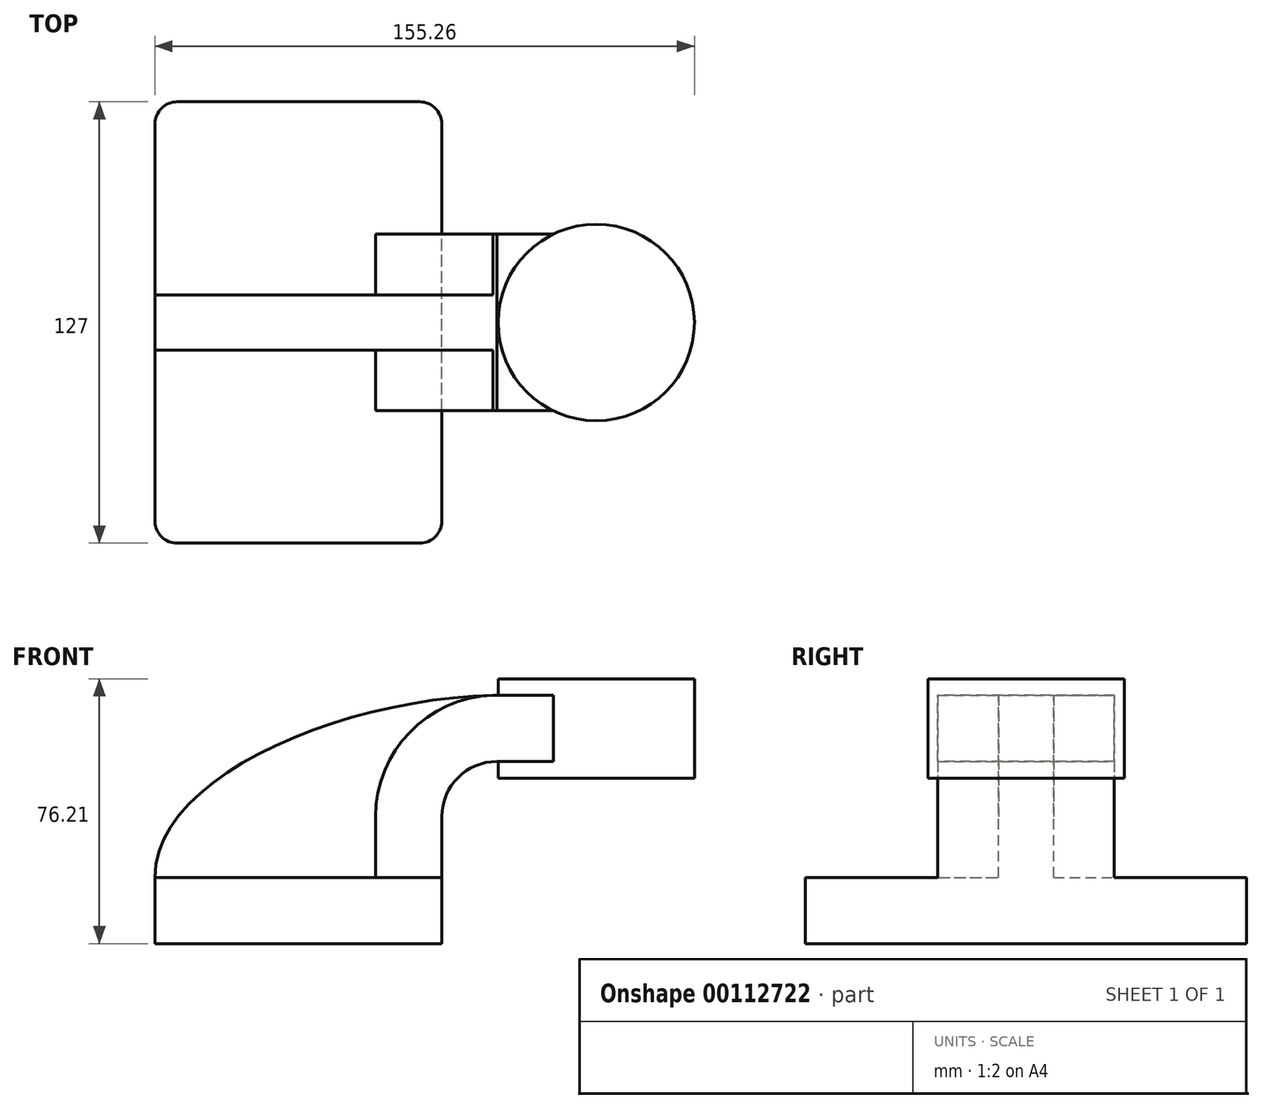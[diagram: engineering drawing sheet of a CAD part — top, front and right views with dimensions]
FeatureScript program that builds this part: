
annotation { "Feature Type Name" : "Feature", "Feature Type Description" : "" }
export const myFeature = defineFeature(function(context is Context, id is Id, definition is map)
    precondition{}
    {
        {
            var Q0;
            Q0=qCreatedBy(makeId("Front.planeOp"),FACE);
            var sketch = newSketch(context, id + "F0", { "sketchPlane" : qUnion([Q0])});
            skLineSegment(sketch, "E0.bottom", {"start": v(-41.28, -9.53) * mm, "end": v(41.28, -9.53) * mm});
            skLineSegment(sketch, "E0.top", {"start": v(-41.28, 9.53) * mm, "end": v(41.28, 9.53) * mm});
            skLineSegment(sketch, "E0.left", {"start": v(-41.28, -9.53) * mm, "end": v(-41.28, 9.53) * mm});
            skLineSegment(sketch, "E0.right", {"start": v(41.28, -9.53) * mm, "end": v(41.28, 9.53) * mm});
            skPoint(sketch, "E0.middle", {"position": v(0, 0) * mm});
            skLineSegment(sketch, "E1.bottom", {"start": v(63.18, 38.1) * mm, "end": v(113.98, 38.1) * mm});
            skLineSegment(sketch, "E1.top", {"start": v(63.18, 66.67) * mm, "end": v(113.98, 66.67) * mm});
            skLineSegment(sketch, "E1.left", {"start": v(63.18, 38.1) * mm, "end": v(63.18, 66.67) * mm});
            skLineSegment(sketch, "E1.right", {"start": v(113.98, 38.1) * mm, "end": v(113.98, 66.67) * mm});
            skPoint(sketch, "E1.middle", {"position": v(88.58, 52.39) * mm});
            skLineSegment(sketch, "E2", {"start": v(41.27, 9.53) * mm, "end": v(41.27, 27) * mm});
            skArc(sketch, "E3", {"start": v(41.27, 27) * mm, "mid": v(45.92, 38.23) * mm, "end": v(57.15, 42.88) * mm});
            skLineSegment(sketch, "E4", {"start": v(57.15, 42.88) * mm, "end": v(85.72, 42.88) * mm});
            skLineSegment(sketch, "E5.0", {"start": v(57.15, 61.93) * mm, "end": v(85.72, 61.93) * mm});
            skArc(sketch, "E5.1", {"start": v(22.23, 27) * mm, "mid": v(32.45, 51.7) * mm, "end": v(57.15, 61.93) * mm});
            skLineSegment(sketch, "E5.2", {"start": v(22.22, 9.53) * mm, "end": v(22.22, 27) * mm});
            skLineSegment(sketch, "E6", {"start": v(85.72, 66.67) * mm, "end": v(85.72, 38.1) * mm});
            skFitSpline(sketch, "E7", {"points": [v(-41.28, 9.53) * mm, v(57.15, 61.93) * mm], "startDerivative": vector(-0.7, 87.75) * mm, "endDerivative": vector(130.7, 1.51) * mm});
            skSolve(sketch);
        }
        {
            var Q0;
            Q0=makeQuery(id+"F0.imprint","IMPRINT",FACE,{"disambiguationData":[TD([[makeQuery(id+"F0.imprint","IMPRINT",EDGE,{"derivedFrom":sQuery(id+"F0.wireOp",EDGE,"E0.bottom")}),1.0]])]});
            extrude(context, id + "F1", {"entities" : qUnion([Q0]), "endBound" : BoundingType.SYMMETRIC, "depth" : 127 * mm});
        }
        {
            var Q0;
            {var subQ1=sQuery(id+"F0.wireOp",EDGE,"E2");Q0=makeQuery(id+"F0.imprint","IMPRINT",FACE,{"disambiguationData":[TD([[makeQuery(id+"F0.imprint","IMPRINT",EDGE,{"derivedFrom":subQ1}),1.0]])]});}
            var Q1;
            {var subQ0=sQuery(id+"F0.wireOp",EDGE,"E4");var subQ1=sQuery(id+"F0.wireOp",EDGE,"E1.left");var subQ2=makeQuery(id+"F0.imprint","INTERSECT",VERTEX,{"derivedFrom":[subQ1,subQ0]});Q1=makeQuery(id+"F0.imprint","IMPRINT",FACE,{"disambiguationData":[TD([[makeQuery(id+"F0.imprint","IMPRINT",EDGE,{"disambiguationData":[TD([[subQ2,-1.0]])],"derivedFrom":subQ1}),-1.0]])]});}
            extrude(context, id + "F2", {"entities" : qUnion([Q0, Q1]), "endBound" : BoundingType.SYMMETRIC, "depth" : 50.8 * mm});
        }
        {
            var Q0;
            {var subQ3=sQuery(id+"F0.wireOp",EDGE,"E5.2");Q0=makeQuery(id+"F0.imprint","IMPRINT",FACE,{"disambiguationData":[TD([[makeQuery(id+"F0.imprint","IMPRINT",EDGE,{"derivedFrom":subQ3}),1.0]])]});}
            extrude(context, id + "F3", {"entities" : qUnion([Q0]), "operationType" : NewBodyOperationType.ADD, "endBound" : BoundingType.SYMMETRIC, "depth" : 15.88 * mm});
        }
        {
            var Q0;
            {var subQ0=sQuery(id+"F0.wireOp",EDGE,"E1.right");Q0=makeQuery(id+"F0.imprint","IMPRINT",FACE,{"disambiguationData":[TD([[makeQuery(id+"F0.imprint","IMPRINT",EDGE,{"derivedFrom":subQ0}),1.0]])]});}
            var Q1;
            Q1=sQuery(id+"F0.wireOp",EDGE,"E6");
            revolve(context, id + "F4", {"operationType" : NewBodyOperationType.ADD, "entities" : qUnion([Q0]), "axis" : qUnion([Q1]), "revolveType" : RevolveType.FULL});
        }
        {
            var Q0;
            Q0=makeQuery(id+"F1.opExtrude","CAP_EDGE",EDGE,{"disambiguationData":[OSD([sQuery(id+"F0.wireOp",EDGE,"E0.right")])],"isStart":false});
            var Q1;
            Q1=makeQuery(id+"F1.opExtrude","CAP_EDGE",EDGE,{"disambiguationData":[OSD([sQuery(id+"F0.wireOp",EDGE,"E0.left")])],"isStart":false});
            var Q2;
            Q2=makeQuery(id+"F1.opExtrude","CAP_EDGE",EDGE,{"disambiguationData":[OSD([sQuery(id+"F0.wireOp",EDGE,"E0.right")])],"isStart":true});
            var Q3;
            Q3=makeQuery(id+"F1.opExtrude","CAP_EDGE",EDGE,{"disambiguationData":[OSD([sQuery(id+"F0.wireOp",EDGE,"E0.left")])],"isStart":true});
            fillet(context, id + "F5", {"entities" : qUnion([Q0, Q1, Q2, Q3]), "radius" : 6.35 * mm, "tangentPropagation" : true, "allowEdgeOverflow" : false});
        }
    });
